# Revit family: 630mm Roof Terminals BIM File
name_source: partatom
category: Air Terminals
units: mm (PartAtom-declared; Revit-internal decimal feet)

## family parameters
Always vertical = Yes
Cut with Voids When Loaded = No
Maintain Annotation Orientation = No
Part Type = Normal
Room Calculation Point = No
Round Connector Dimension = Use Diameter
Shared = No
Work Plane-Based = No

## types (2) — shared parameters
Cap dimensions (mm) = 780x1000
Cap height (mm) = 160
Connection diameter = 630 mm  [stored 2.06693 ft]
Extract air flow at 20 Pa (m3/h) = 8000
Flow rate = 1250.0 L/s
Installation instructions URL link = https://www.airflow.com
Lead dimensions (mm) = 1200x1000
Manufacturer = Airflow
Manufacturer's URL link = http://www.airflow.com
Material 1 = ANJ010016 1
Material 2 = ANJ010016 2
Material 4 = ANJ010016 4
Pressure = 100.0 Pa
Product URL link = https://www.airflow.com
Roof height (mm) = 215
Supply air flow at 20 Pa (m3/h) = 4500
URL = http://www.airflow.com
zero-valued in all types: Default Elevation

## per-type parameters (varying)
| type | Manufacturer's name | Material 3 | Part number |
| 630mm Terracotta Roof Terminal | Airlfow | ANJ010016 3 | 90001416 |
| 630mm Slate Roof Terminal | Airflow | ANJ010016 3' | 90001415 |

note: column(s) folded — value = type name in every type: Model, Product name

note: [stored X ft] marks values corroborated as IEEE doubles in the binary element streams (Revit-internal decimal feet)

## geometry (parser evidence)
native form markers: Sweep x5
no freeform markers — native parametric forms only
